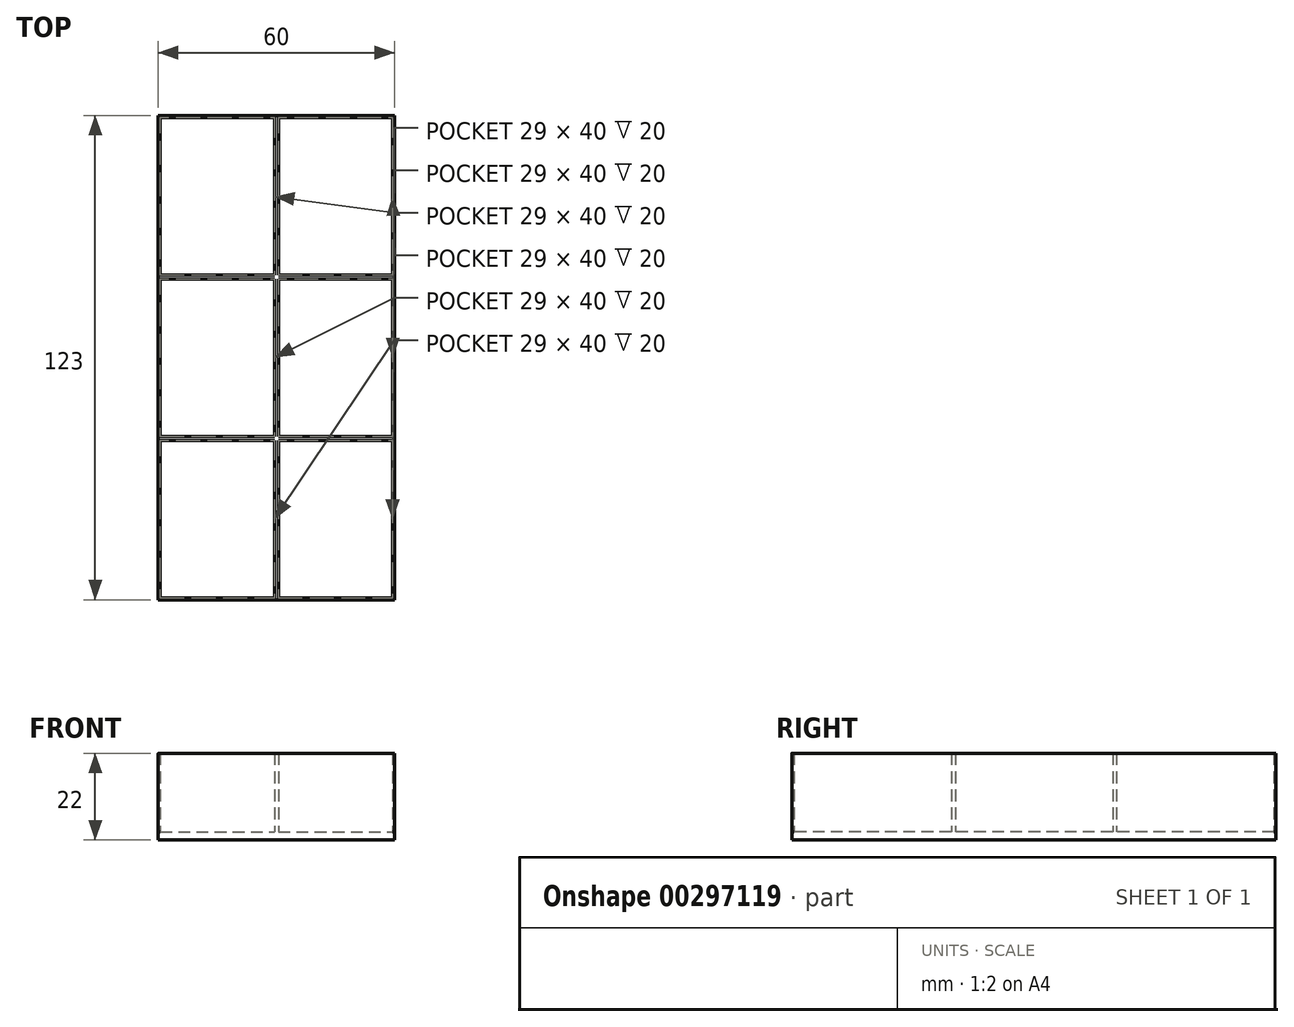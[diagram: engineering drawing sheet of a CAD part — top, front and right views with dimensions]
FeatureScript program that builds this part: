
annotation { "Feature Type Name" : "Feature", "Feature Type Description" : "" }
export const myFeature = defineFeature(function(context is Context, id is Id, definition is map)
    precondition{}
    {
        {
            var Q0;
            Q0=qCreatedBy(makeId("Top.planeOp"),FACE);
            var sketch = newSketch(context, id + "F0", { "sketchPlane" : qUnion([Q0])});
            skLineSegment(sketch, "E0.bottom", {"start": v(-30, 61.5) * mm, "end": v(30, 61.5) * mm});
            skLineSegment(sketch, "E0.top", {"start": v(-30, -61.5) * mm, "end": v(30, -61.5) * mm});
            skLineSegment(sketch, "E0.left", {"start": v(-30, 61.5) * mm, "end": v(-30, -61.5) * mm});
            skLineSegment(sketch, "E0.right", {"start": v(30, 61.5) * mm, "end": v(30, -61.5) * mm});
            skPoint(sketch, "E0.middle", {"position": v(0, 0) * mm});
            skLineSegment(sketch, "E1", {"start": v(-30, 61.5) * mm, "end": v(-30, 20.5) * mm});
            skLineSegment(sketch, "E2", {"start": v(-30, -61.5) * mm, "end": v(-30, -20.5) * mm});
            skLineSegment(sketch, "E3.bottom", {"start": v(-30, 61.5) * mm, "end": v(0, 61.5) * mm});
            skLineSegment(sketch, "E4", {"start": v(-15, 61.5) * mm, "end": v(-15, 61) * mm});
            skLineSegment(sketch, "E5", {"start": v(0, -61.5) * mm, "end": v(15, -61.5) * mm});
            skLineSegment(sketch, "E6.bottom", {"start": v(-29.5, 61) * mm, "end": v(-0.5, 61) * mm});
            skLineSegment(sketch, "E6.top", {"start": v(-29.5, 21) * mm, "end": v(-0.5, 21) * mm});
            skLineSegment(sketch, "E6.left", {"start": v(-29.5, 61) * mm, "end": v(-29.5, 21) * mm});
            skLineSegment(sketch, "E6.right", {"start": v(-0.5, 61) * mm, "end": v(-0.5, 21) * mm});
            skPoint(sketch, "E6.middle", {"position": v(-15, 41) * mm});
            skPoint(sketch, "E6.middle.positionSnap0", {"position": v(-30, 41) * mm});
            skPoint(sketch, "E6.centerSnap0", {"position": v(-30, 41) * mm});
            skLineSegment(sketch, "E7.bottom", {"start": v(0.5, 61) * mm, "end": v(29.5, 61) * mm});
            skLineSegment(sketch, "E7.top", {"start": v(0.5, 21) * mm, "end": v(29.5, 21) * mm});
            skLineSegment(sketch, "E7.left", {"start": v(0.5, 61) * mm, "end": v(0.5, 21) * mm});
            skLineSegment(sketch, "E7.right", {"start": v(29.5, 61) * mm, "end": v(29.5, 21) * mm});
            skPoint(sketch, "E7.middle", {"position": v(15, 41) * mm});
            skPoint(sketch, "E7.middle.positionSnap0", {"position": v(0, 41) * mm});
            skPoint(sketch, "E7.centerSnap0", {"position": v(0, 41) * mm});
            skLineSegment(sketch, "E8.bottom", {"start": v(0.5, 20) * mm, "end": v(29.5, 20) * mm});
            skLineSegment(sketch, "E8.top", {"start": v(0.5, -20) * mm, "end": v(29.5, -20) * mm});
            skLineSegment(sketch, "E8.left", {"start": v(0.5, 20) * mm, "end": v(0.5, -20) * mm});
            skLineSegment(sketch, "E8.right", {"start": v(29.5, 20) * mm, "end": v(29.5, -20) * mm});
            skPoint(sketch, "E8.middle", {"position": v(15, 0) * mm});
            skLineSegment(sketch, "E9.bottom", {"start": v(-29.5, 20) * mm, "end": v(-0.5, 20) * mm});
            skLineSegment(sketch, "E9.top", {"start": v(-29.5, -20) * mm, "end": v(-0.5, -20) * mm});
            skLineSegment(sketch, "E9.left", {"start": v(-29.5, 20) * mm, "end": v(-29.5, -20) * mm});
            skLineSegment(sketch, "E9.right", {"start": v(-0.5, 20) * mm, "end": v(-0.5, -20) * mm});
            skPoint(sketch, "E9.middle", {"position": v(-15, 0) * mm});
            skLineSegment(sketch, "E10.bottom", {"start": v(-29.5, -21) * mm, "end": v(-0.5, -21) * mm});
            skLineSegment(sketch, "E10.top", {"start": v(-29.5, -61) * mm, "end": v(-0.5, -61) * mm});
            skLineSegment(sketch, "E10.left", {"start": v(-29.5, -21) * mm, "end": v(-29.5, -61) * mm});
            skLineSegment(sketch, "E10.right", {"start": v(-0.5, -21) * mm, "end": v(-0.5, -61) * mm});
            skPoint(sketch, "E10.middle", {"position": v(-15, -41) * mm});
            skPoint(sketch, "E10.middle.positionSnap0", {"position": v(-30, -41) * mm});
            skPoint(sketch, "E10.cornerSnap0", {"position": v(-29.5, 0) * mm});
            skPoint(sketch, "E10.centerSnap0", {"position": v(-30, -41) * mm});
            skLineSegment(sketch, "E11.bottom", {"start": v(0.5, -21) * mm, "end": v(29.5, -21) * mm});
            skLineSegment(sketch, "E11.top", {"start": v(0.5, -61) * mm, "end": v(29.5, -61) * mm});
            skLineSegment(sketch, "E11.left", {"start": v(0.5, -21) * mm, "end": v(0.5, -61) * mm});
            skLineSegment(sketch, "E11.right", {"start": v(29.5, -21) * mm, "end": v(29.5, -61) * mm});
            skPoint(sketch, "E11.middle", {"position": v(15, -41) * mm});
            skPoint(sketch, "E11.middle.positionSnap0", {"position": v(-0.5, -41) * mm});
            skPoint(sketch, "E11.cornerSnap0", {"position": v(-15, -21) * mm});
            skPoint(sketch, "E11.centerSnap0", {"position": v(-0.5, -41) * mm});
            skLineSegment(sketch, "E12.trimOffspring", {"start": v(15, 61) * mm, "end": v(15, 61.5) * mm});
            skPoint(sketch, "E13.orphan", {"position": v(0, 20.5) * mm});
            skPoint(sketch, "E14.trimOffspring.end.orphan", {"position": v(30, 20.5) * mm});
            skLineSegment(sketch, "E15.trimOffspring", {"start": v(15, -21) * mm, "end": v(15, -20) * mm});
            skPoint(sketch, "E16.trimOffspring.end.orphan", {"position": v(-15, -61.5) * mm});
            skPoint(sketch, "E17.start.orphan", {"position": v(0, 61.5) * mm});
            skSolve(sketch);
        }
        {
            var Q0;
            Q0 = qSketchRegion(id + "F0", true);
            extrude(context, id + "F1", {"entities" : qUnion([Q0]), "depth" : 20 * mm});
        }
        {
            var Q0;
            Q0=makeQuery(id+"F1.opExtrude","SWEPT_EDGE",EDGE,{"disambiguationData":[OSD([sQuery(id+"F0.wireOp",EDGE,"E0.bottom"),sQuery(id+"F0.wireOp",EDGE,"E0.right")])]});
            var Q1;
            Q1=makeQuery(id+"F1.opExtrude","SWEPT_EDGE",EDGE,{"disambiguationData":[OSD([sQuery(id+"F0.wireOp",EDGE,"E0.top"),sQuery(id+"F0.wireOp",EDGE,"E0.right")])]});
            var Q2;
            Q2=makeQuery(id+"F1.opExtrude","SWEPT_EDGE",EDGE,{"disambiguationData":[OSD([sQuery(id+"F0.wireOp",EDGE,"E0.top"),sQuery(id+"F0.wireOp",EDGE,"E2")])]});
            var Q3;
            Q3=makeQuery(id+"F1.opExtrude","SWEPT_EDGE",EDGE,{"disambiguationData":[OSD([sQuery(id+"F0.wireOp",EDGE,"E3.bottom"),sQuery(id+"F0.wireOp",EDGE,"E1")])]});
            fillet(context, id + "F2", {"entities" : qUnion([Q0, Q1, Q2, Q3]), "radius" : 0.5 * mm, "tangentPropagation" : true, "allowEdgeOverflow" : false});
        }
        {
            var Q0;
            Q0=qCreatedBy(makeId("Top.planeOp"),FACE);
            var sketch = newSketch(context, id + "F3", { "sketchPlane" : qUnion([Q0])});
            skLineSegment(sketch, "E18.bottom", {"start": v(-30, -61.5) * mm, "end": v(30, -61.5) * mm});
            skLineSegment(sketch, "E18.top", {"start": v(-30, 61.5) * mm, "end": v(30, 61.5) * mm});
            skLineSegment(sketch, "E18.left", {"start": v(-30, -61.5) * mm, "end": v(-30, 61.5) * mm});
            skLineSegment(sketch, "E18.right", {"start": v(30, -61.5) * mm, "end": v(30, 61.5) * mm});
            skPoint(sketch, "E18.middle", {"position": v(0, 0) * mm});
            skSolve(sketch);
        }
        {
            var Q0;
            Q0 = qSketchRegion(id + "F3", true);
            extrude(context, id + "F4", {"entities" : qUnion([Q0]), "operationType" : NewBodyOperationType.ADD, "oppositeDirection" : true, "depth" : 2 * mm});
        }
    });
